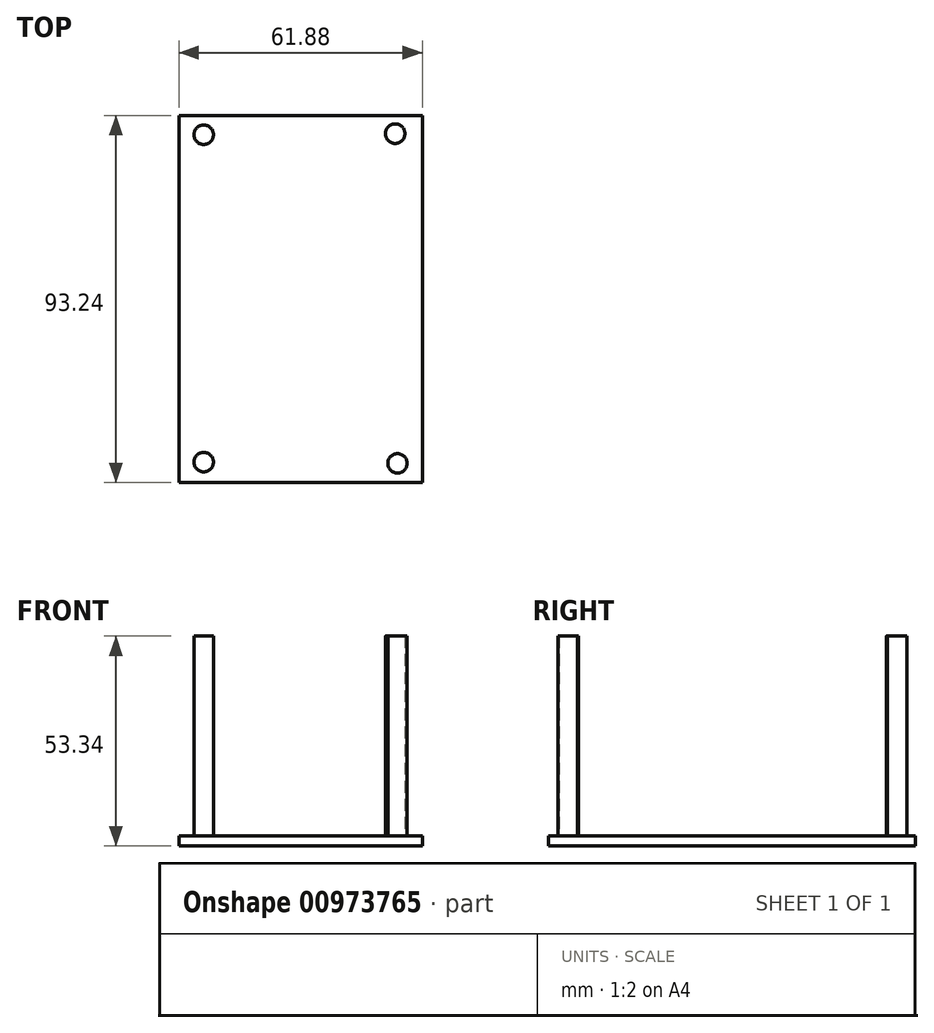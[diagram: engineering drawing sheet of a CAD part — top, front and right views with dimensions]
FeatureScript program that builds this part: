
annotation { "Feature Type Name" : "Feature", "Feature Type Description" : "" }
export const myFeature = defineFeature(function(context is Context, id is Id, definition is map)
    precondition{}
    {
        {
            var Q0;
            Q0=qCreatedBy(makeId("Top.planeOp"),FACE);
            var sketch = newSketch(context, id + "F0", { "sketchPlane" : qUnion([Q0])});
            skLineSegment(sketch, "E0.bottom", {"start": v(-30.94, 40.72) * mm, "end": v(30.94, 40.72) * mm});
            skLineSegment(sketch, "E0.top", {"start": v(-30.94, -52.52) * mm, "end": v(30.94, -52.52) * mm});
            skLineSegment(sketch, "E0.left", {"start": v(-30.94, 40.72) * mm, "end": v(-30.94, -52.52) * mm});
            skLineSegment(sketch, "E0.right", {"start": v(30.94, 40.72) * mm, "end": v(30.94, -52.52) * mm});
            skSolve(sketch);
        }
        {
            var Q0;
            Q0 = qSketchRegion(id + "F0", true);
            extrude(context, id + "F1", {"entities" : qUnion([Q0]), "depth" : 2.54 * mm, "offsetDistance" : 25.4 * mm});
        }
        {
            var Q0;
            Q0=makeQuery(id+"F1.opExtrude","CAP_FACE",FACE,{"disambiguationData":[OSD([sQuery(id+"F0.wireOp",EDGE,"E0.bottom"),sQuery(id+"F0.wireOp",EDGE,"E0.top"),sQuery(id+"F0.wireOp",EDGE,"E0.left"),sQuery(id+"F0.wireOp",EDGE,"E0.right")])],"isStart":true});
            var sketch = newSketch(context, id + "F2", { "sketchPlane" : qUnion([Q0])});
            skCircle(sketch, "E1", {"center": v(-24.32, 47.63) * mm, "radius": 3.36 * mm});
            skSolve(sketch);
        }
        {
            var Q0;
            Q0 = qSketchRegion(id + "F2", true);
            extrude(context, id + "F3", {"entities" : qUnion([Q0]), "operationType" : NewBodyOperationType.REMOVE, "depth" : 34.3 * mm, "offsetDistance" : 25.4 * mm});
        }
        {
            var Q0;
            Q0=makeQuery(id+"F1.opExtrude","CAP_FACE",FACE,{"disambiguationData":[OSD([sQuery(id+"F0.wireOp",EDGE,"E0.bottom"),sQuery(id+"F0.wireOp",EDGE,"E0.top"),sQuery(id+"F0.wireOp",EDGE,"E0.left"),sQuery(id+"F0.wireOp",EDGE,"E0.right")])],"isStart":false});
            var sketch = newSketch(context, id + "F4", { "sketchPlane" : qUnion([Q0])});
            skCircle(sketch, "E2", {"center": v(-24.6, 35.83) * mm, "radius": 2.48 * mm});
            skSolve(sketch);
        }
        {
            var Q0;
            Q0 = qSketchRegion(id + "F4", true);
            extrude(context, id + "F5", {"entities" : qUnion([Q0]), "operationType" : NewBodyOperationType.ADD, "depth" : 50.8 * mm, "offsetDistance" : 25.4 * mm});
        }
        {
            var Q0;
            Q0=makeQuery(id+"F1.opExtrude","CAP_FACE",FACE,{"disambiguationData":[OSD([sQuery(id+"F0.wireOp",EDGE,"E0.bottom"),sQuery(id+"F0.wireOp",EDGE,"E0.top"),sQuery(id+"F0.wireOp",EDGE,"E0.left"),sQuery(id+"F0.wireOp",EDGE,"E0.right")])],"isStart":false});
            var sketch = newSketch(context, id + "F6", { "sketchPlane" : qUnion([Q0])});
            skCircle(sketch, "E3", {"center": v(24.03, 36.12) * mm, "radius": 2.48 * mm});
            skSolve(sketch);
        }
        {
            var Q0;
            Q0 = qSketchRegion(id + "F6", true);
            extrude(context, id + "F7", {"entities" : qUnion([Q0]), "operationType" : NewBodyOperationType.ADD, "depth" : 50.8 * mm, "offsetDistance" : 25.4 * mm});
        }
        {
            var Q0;
            Q0=makeQuery(id+"F1.opExtrude","CAP_FACE",FACE,{"disambiguationData":[OSD([sQuery(id+"F0.wireOp",EDGE,"E0.bottom"),sQuery(id+"F0.wireOp",EDGE,"E0.top"),sQuery(id+"F0.wireOp",EDGE,"E0.left"),sQuery(id+"F0.wireOp",EDGE,"E0.right")])],"isStart":false});
            var sketch = newSketch(context, id + "F8", { "sketchPlane" : qUnion([Q0])});
            skCircle(sketch, "E4", {"center": v(-24.6, -47.34) * mm, "radius": 2.48 * mm});
            skSolve(sketch);
        }
        {
            var Q0;
            Q0 = qSketchRegion(id + "F8", true);
            extrude(context, id + "F9", {"entities" : qUnion([Q0]), "operationType" : NewBodyOperationType.ADD, "depth" : 50.8 * mm, "offsetDistance" : 25.4 * mm});
        }
        {
            var Q0;
            Q0=makeQuery(id+"F1.opExtrude","CAP_FACE",FACE,{"disambiguationData":[OSD([sQuery(id+"F0.wireOp",EDGE,"E0.bottom"),sQuery(id+"F0.wireOp",EDGE,"E0.top"),sQuery(id+"F0.wireOp",EDGE,"E0.left"),sQuery(id+"F0.wireOp",EDGE,"E0.right")])],"isStart":false});
            var sketch = newSketch(context, id + "F10", { "sketchPlane" : qUnion([Q0])});
            skCircle(sketch, "E5", {"center": v(24.6, -47.63) * mm, "radius": 2.46 * mm});
            skSolve(sketch);
        }
        {
            var Q0;
            Q0 = qSketchRegion(id + "F10", true);
            extrude(context, id + "F11", {"entities" : qUnion([Q0]), "operationType" : NewBodyOperationType.ADD, "depth" : 50.8 * mm, "offsetDistance" : 25.4 * mm});
        }
    });
